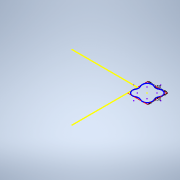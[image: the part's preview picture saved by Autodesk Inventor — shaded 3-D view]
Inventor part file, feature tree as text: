
AUTODESK INVENTOR PART (.ipt)
format: ipt  version: 2021 (Build 250183000, 183)  size: 94,208 bytes
history: native  units: in
note: dims shown in document units (in); Inventor stores cm internally (conversion verified against a paired STEP export)
features: sketch x1
ambient origin geometry x8: Origin, YZ Plane, XZ Plane, XY Plane, X Axis, Y Axis, Z Axis, Center Point
feature tree (1):
  sketch  "Boceto1"  dims[d0=5.9055in d1=5.9055in]
